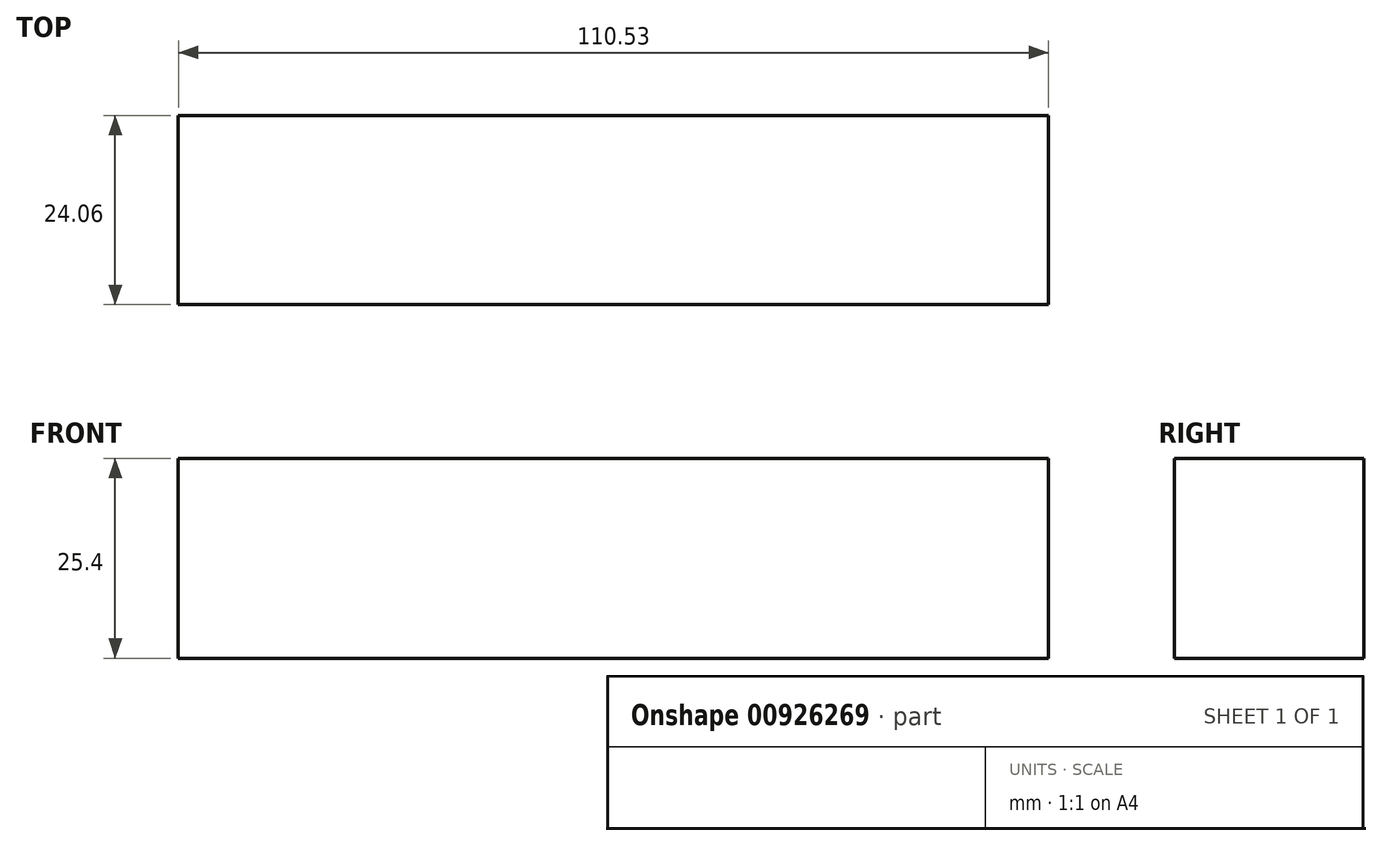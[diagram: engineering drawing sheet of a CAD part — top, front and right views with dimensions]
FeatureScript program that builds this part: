
annotation { "Feature Type Name" : "Feature", "Feature Type Description" : "" }
export const myFeature = defineFeature(function(context is Context, id is Id, definition is map)
    precondition{}
    {
        {
            var Q0;
            Q0=qCreatedBy(makeId("Top.planeOp"),FACE);
            var sketch = newSketch(context, id + "F0", { "sketchPlane" : qUnion([Q0])});
            skLineSegment(sketch, "E0.bottom", {"start": v(0, 0) * mm, "end": v(0, 0) * mm});
            skLineSegment(sketch, "E0.top", {"start": v(0, -3.27) * mm, "end": v(0, -3.27) * mm});
            skLineSegment(sketch, "E0.left", {"start": v(0, 0) * mm, "end": v(0, -3.27) * mm});
            skLineSegment(sketch, "E0.right", {"start": v(0, 0) * mm, "end": v(0, -3.27) * mm});
            skLineSegment(sketch, "E1.bottom", {"start": v(0, 0) * mm, "end": v(-110.53, 0) * mm});
            skLineSegment(sketch, "E1.top", {"start": v(0, 24.06) * mm, "end": v(-110.53, 24.06) * mm});
            skLineSegment(sketch, "E1.left", {"start": v(0, 0) * mm, "end": v(0, 24.06) * mm});
            skLineSegment(sketch, "E1.right", {"start": v(-110.53, 0) * mm, "end": v(-110.53, 24.06) * mm});
            skSolve(sketch);
        }
        {
            var Q0;
            Q0 = qSketchRegion(id + "F0", true);
            extrude(context, id + "F1", {"entities" : qUnion([Q0]), "depth" : 25.4 * mm, "offsetDistance" : 25.4 * mm});
        }
    });
